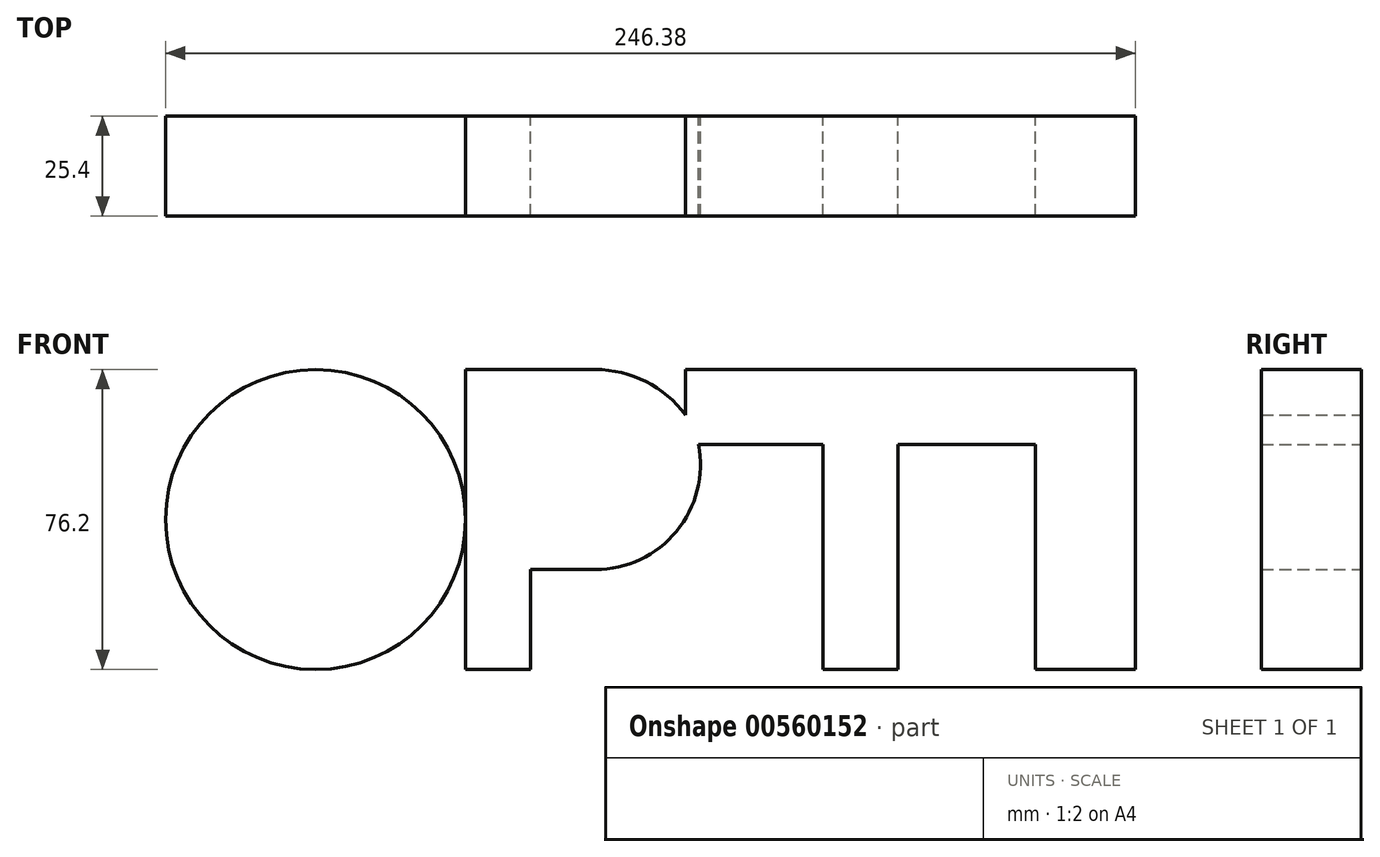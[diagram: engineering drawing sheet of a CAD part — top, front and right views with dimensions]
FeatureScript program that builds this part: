
annotation { "Feature Type Name" : "Feature", "Feature Type Description" : "" }
export const myFeature = defineFeature(function(context is Context, id is Id, definition is map)
    precondition{}
    {
        {
            var Q0;
            Q0=qCreatedBy(makeId("Front.planeOp"),FACE);
            var sketch = newSketch(context, id + "F0", { "sketchPlane" : qUnion([Q0])});
            skCircle(sketch, "E0", {"center": v(0, 0) * mm, "radius": 38.1 * mm});
            skLineSegment(sketch, "E1", {"start": v(38.1, 0) * mm, "end": v(38.1, 38.1) * mm});
            skLineSegment(sketch, "E2", {"start": v(38.1, 38.1) * mm, "end": v(54.6, 38.1) * mm});
            skLineSegment(sketch, "E3", {"start": v(54.6, -38.1) * mm, "end": v(38.1, -38.1) * mm});
            skLineSegment(sketch, "E4", {"start": v(38.1, -38.1) * mm, "end": v(38.1, 0) * mm});
            skLineSegment(sketch, "E5", {"start": v(54.6, 38.1) * mm, "end": v(71.12, 38.1) * mm});
            skLineSegment(sketch, "E6", {"start": v(71.12, -12.7) * mm, "end": v(54.6, -12.7) * mm});
            skLineSegment(sketch, "E7", {"start": v(54.6, -12.7) * mm, "end": v(54.6, -38.1) * mm});
            skLineSegment(sketch, "E8.bottom", {"start": v(93.98, 38.1) * mm, "end": v(182.88, 38.1) * mm});
            skLineSegment(sketch, "E9.bottom", {"start": v(128.9, -38.1) * mm, "end": v(147.96, -38.1) * mm});
            skLineSegment(sketch, "E9.left", {"start": v(128.9, -38.1) * mm, "end": v(128.9, 19.05) * mm});
            skLineSegment(sketch, "E9.right", {"start": v(147.96, -38.1) * mm, "end": v(147.96, 19.05) * mm});
            skLineSegment(sketch, "E10", {"start": v(147.96, 19.05) * mm, "end": v(182.88, 19.05) * mm});
            skLineSegment(sketch, "E11", {"start": v(128.9, 19.05) * mm, "end": v(97.27, 19.05) * mm});
            skLineSegment(sketch, "E12", {"start": v(93.98, 38.1) * mm, "end": v(93.98, 26.54) * mm});
            skArc(sketch, "E13", {"start": v(71.12, -12.7) * mm, "mid": v(91.69, -3) * mm, "end": v(97.27, 19.05) * mm});
            skArc(sketch, "E14", {"start": v(93.98, 26.54) * mm, "mid": v(83.93, 35.05) * mm, "end": v(71.12, 38.1) * mm});
            skLineSegment(sketch, "E15.bottom", {"start": v(182.88, 38.1) * mm, "end": v(208.28, 38.1) * mm});
            skLineSegment(sketch, "E15.top", {"start": v(182.88, -38.1) * mm, "end": v(208.28, -38.1) * mm});
            skLineSegment(sketch, "E16", {"start": v(182.88, -38.1) * mm, "end": v(182.88, 19.05) * mm});
            skLineSegment(sketch, "E17", {"start": v(208.28, 38.1) * mm, "end": v(208.28, -38.1) * mm});
            skSolve(sketch);
        }
        {
            var Q0;
            Q0 = qSketchRegion(id + "F0", true);
            extrude(context, id + "F1", {"entities" : qUnion([Q0]), "depth" : 25.4 * mm, "offsetDistance" : 25.4 * mm});
        }
    });
